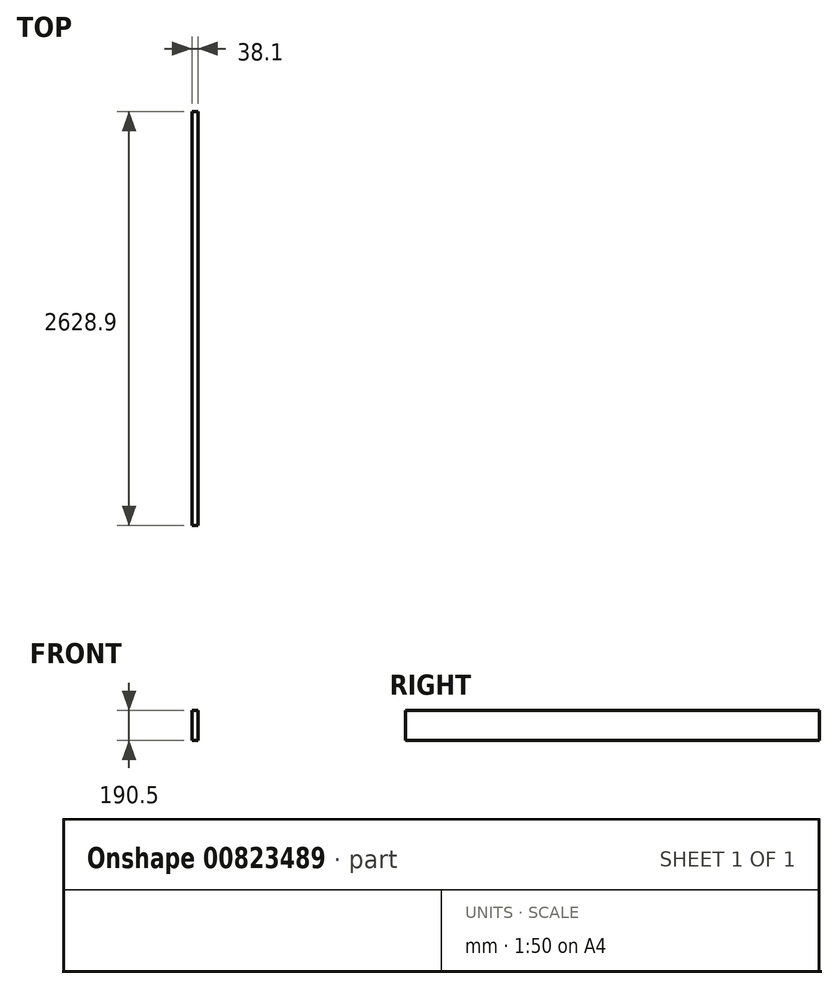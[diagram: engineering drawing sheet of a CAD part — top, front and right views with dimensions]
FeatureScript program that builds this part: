
annotation { "Feature Type Name" : "Feature", "Feature Type Description" : "" }
export const myFeature = defineFeature(function(context is Context, id is Id, definition is map)
    precondition{}
    {
        {
            var Q0;
            Q0=qCreatedBy(makeId("Front.planeOp"),FACE);
            var sketch = newSketch(context, id + "F0", { "sketchPlane" : qUnion([Q0])});
            skLineSegment(sketch, "E0.bottom", {"start": v(0, 0) * mm, "end": v(38.1, 0) * mm});
            skLineSegment(sketch, "E0.top", {"start": v(0, 190.5) * mm, "end": v(38.1, 190.5) * mm});
            skLineSegment(sketch, "E0.left", {"start": v(0, 0) * mm, "end": v(0, 190.5) * mm});
            skLineSegment(sketch, "E0.right", {"start": v(38.1, 0) * mm, "end": v(38.1, 190.5) * mm});
            skSolve(sketch);
        }
        {
            var Q0;
            Q0=qSketchRegion(id+"F0",true);
            extrude(context, id + "F1", {"entities" : qUnion([Q0]), "depth" : 2628.9 * mm, "offsetDistance" : 25.4 * mm});
        }
    });
